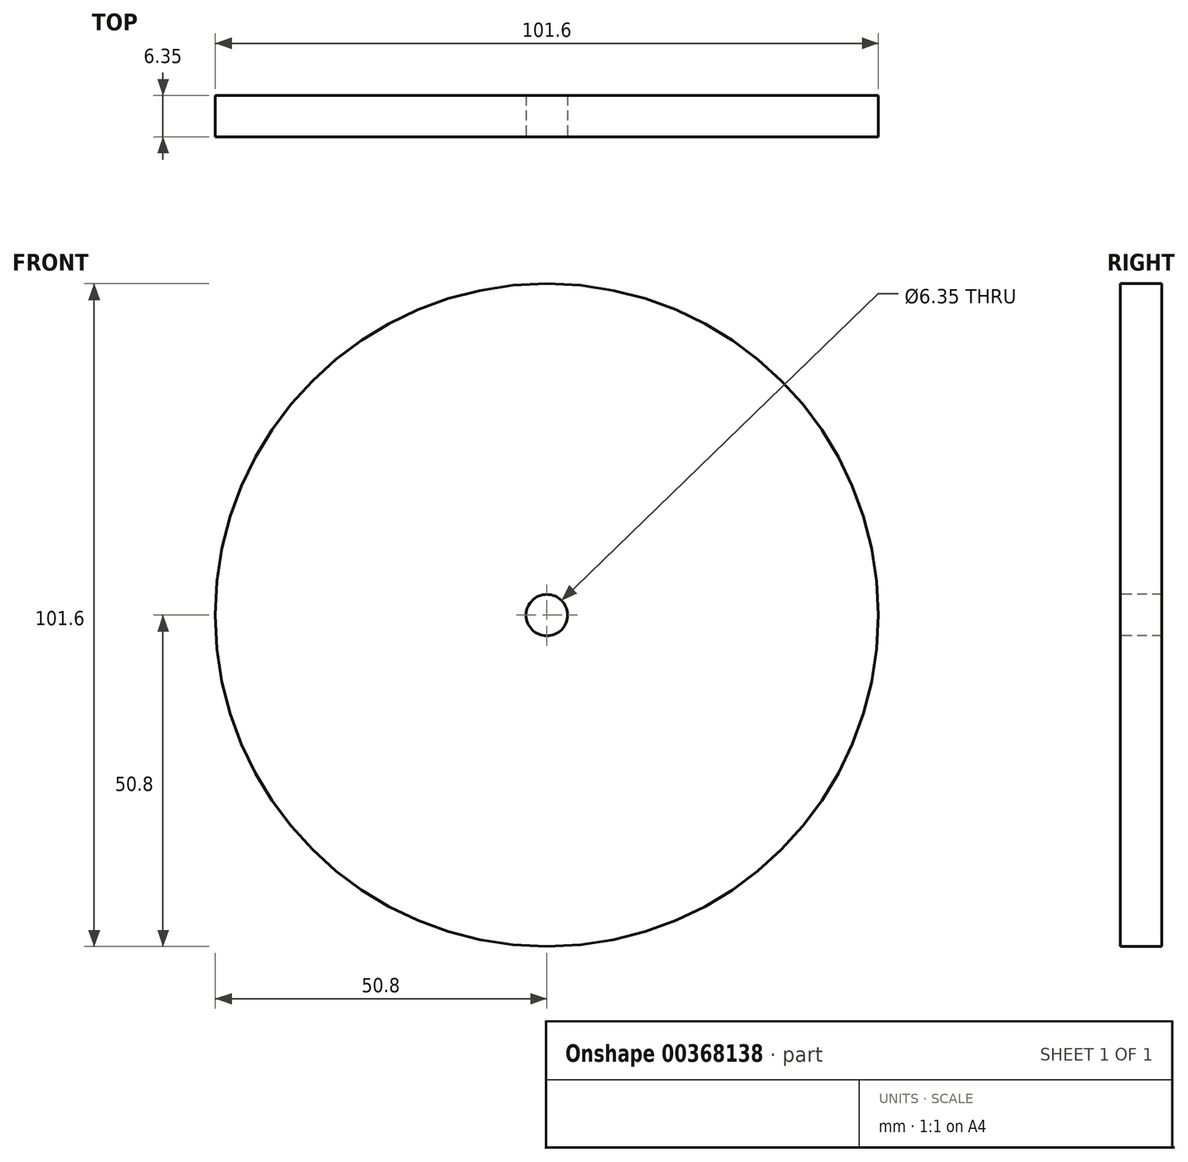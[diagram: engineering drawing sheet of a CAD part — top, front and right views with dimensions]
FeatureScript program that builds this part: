
annotation { "Feature Type Name" : "Feature", "Feature Type Description" : "" }
export const myFeature = defineFeature(function(context is Context, id is Id, definition is map)
    precondition{}
    {
        {
            var Q0;
            Q0=qCreatedBy(makeId("Front.planeOp"),FACE);
            var sketch = newSketch(context, id + "F0", { "sketchPlane" : qUnion([Q0])});
            skCircle(sketch, "E0", {"center": v(0, 0) * mm, "radius": 50.8 * mm});
            skSolve(sketch);
        }
        {
            var Q0;
            Q0=makeQuery(id+"F0.imprint","IMPRINT",FACE,{"disambiguationData":[TD([[makeQuery(id+"F0.imprint","IMPRINT",EDGE,{"derivedFrom":sQuery(id+"F0.wireOp",EDGE,"E0")}),1.0]])]});
            extrude(context, id + "F1", {"entities" : qUnion([Q0]), "depth" : 6.35 * mm, "offsetDistance" : 25.4 * mm});
        }
        {
            var Q0;
            Q0=makeQuery(id+"F1.opExtrude","CAP_FACE",FACE,{"disambiguationData":[OSD([sQuery(id+"F0.wireOp",EDGE,"E0")])],"isStart":false});
            var sketch = newSketch(context, id + "F2", { "sketchPlane" : qUnion([Q0])});
            skCircle(sketch, "E1", {"center": v(0, 0) * mm, "radius": 3.17 * mm});
            skSolve(sketch);
        }
        {
            var Q0;
            Q0=makeQuery(id+"F2.imprint","IMPRINT",FACE,{"disambiguationData":[TD([[makeQuery(id+"F2.imprint","IMPRINT",EDGE,{"derivedFrom":sQuery(id+"F2.wireOp",EDGE,"E1")}),1.0]])]});
            extrude(context, id + "F3", {"entities" : qUnion([Q0]), "operationType" : NewBodyOperationType.REMOVE, "oppositeDirection" : true, "depth" : 6.35 * mm});
        }
    });
